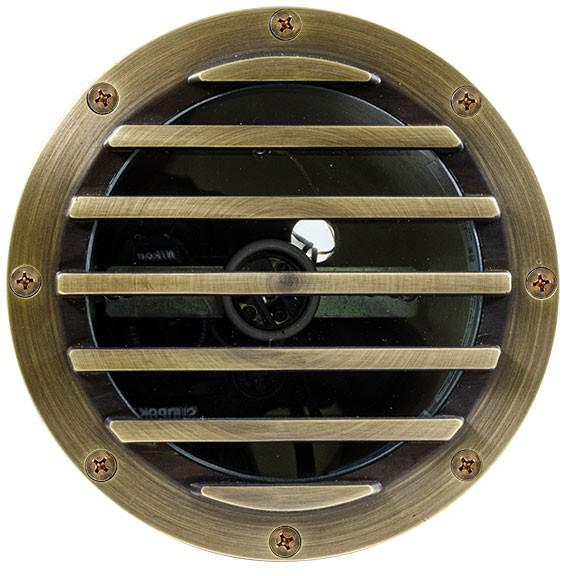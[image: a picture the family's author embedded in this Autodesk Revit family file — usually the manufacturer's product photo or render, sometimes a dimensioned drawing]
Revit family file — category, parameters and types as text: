
# Revit family: Alcon-9150-D180-Revit-Family
name_source: partatom
category: Luminarias
units: mm (PartAtom-declared; Revit-internal decimal feet)

## family parameters
Anfitrión = Cara
Compartido = No
Corte con vacíos al cargar = No
Cota de conector redondo = Usar diámetro
Mantener orientación de anotación = No
Origen de luz = Sí
Punto de cálculo de habitación = No
Tipo de pieza = Normal

## types (1)
- Alcon-9150-D180-Revit-Family
    Cambio de temperatura de color de luz atenuada = <Ninguno>
    Elevación por defecto = 4' - 0"
    Fabricante = Alcon Lighting
    Filtro de color = 16777215
    GLASS LENS = Analytical Panels
    HOUSING = <Por categoría>
    LENS GLASS = Glass
    Link to IES File = https://www.alconlighting.com
    Longitud de símbolo de origen de luz = 10' - 0"
    Modelo = Alcon Lighting 9150-D180
    Product Data URL = https://www.alconlighting.com
    Product Page = https://www.alconlighting.com
    TAP LENS = <Por categoría>
    TOP FINISH = <Por categoría>
    URL = https://www.alconlighting.com
    Ángulo de campo de foco = 90.00°
    Ángulo de enfoque = 30.00°
    Ángulo de inclinación = 60.00°

## geometry (parser evidence)
native form markers: Sweep x3
no freeform markers — native parametric forms only
